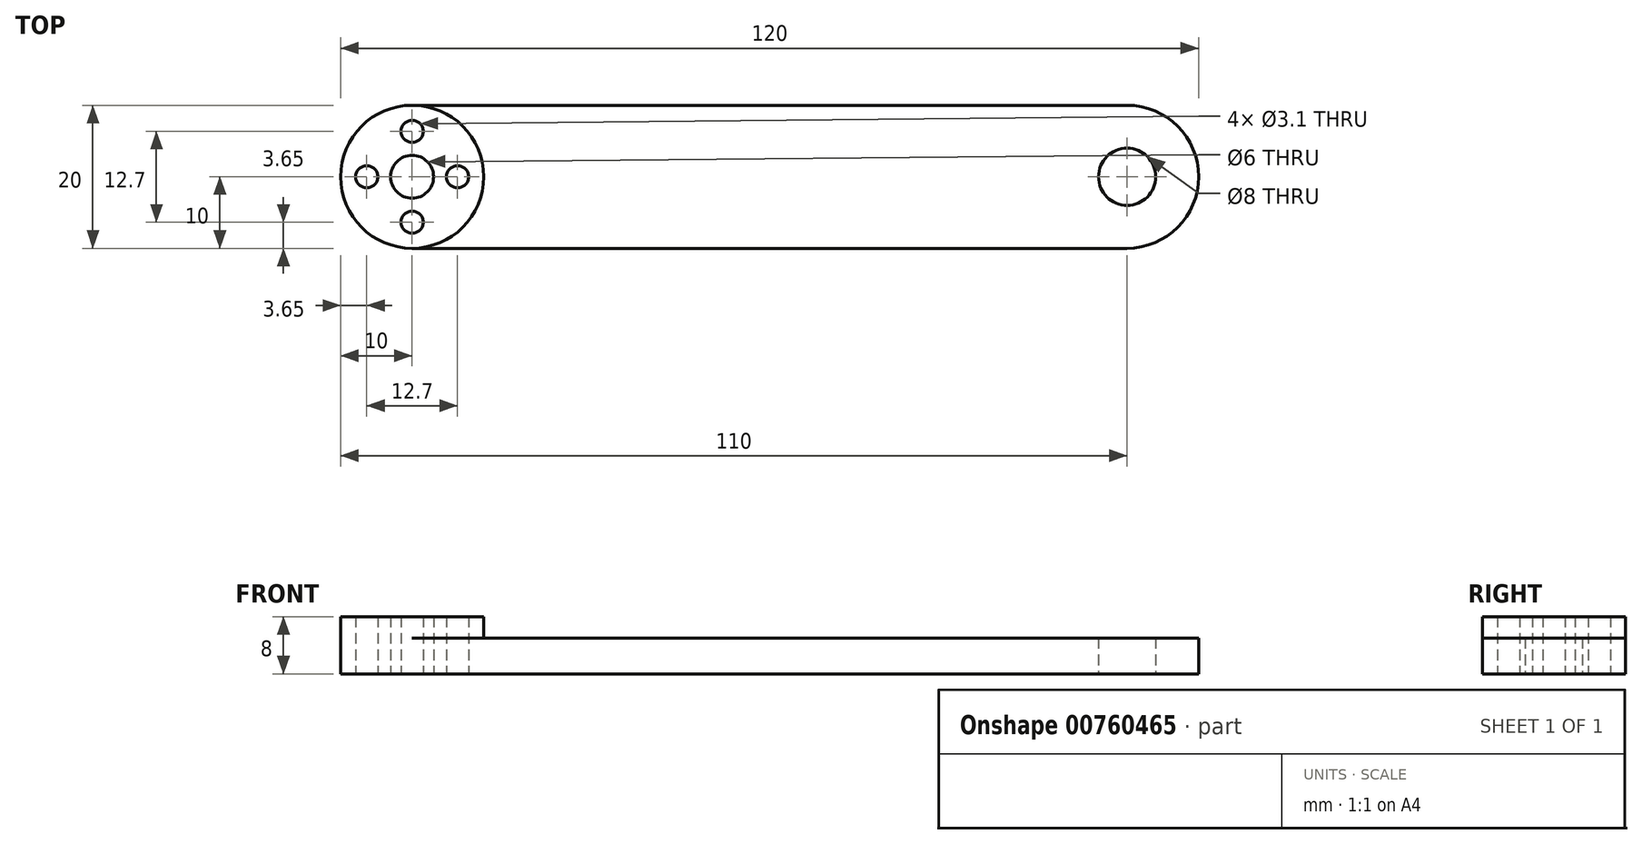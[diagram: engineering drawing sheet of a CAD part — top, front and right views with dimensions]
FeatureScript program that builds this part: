
annotation { "Feature Type Name" : "Feature", "Feature Type Description" : "" }
export const myFeature = defineFeature(function(context is Context, id is Id, definition is map)
    precondition{}
    {
        {
            var Q0;
            Q0=qCreatedBy(makeId("Top.planeOp"),FACE);
            var sketch = newSketch(context, id + "F0", { "sketchPlane" : qUnion([Q0])});
            skCircle(sketch, "E0", {"center": v(0, 0) * mm, "radius": 10 * mm});
            skCircle(sketch, "E1", {"center": v(6.35, 0) * mm, "radius": 1.55 * mm});
            skCircle(sketch, "E2.1.0", {"center": v(0, 6.35) * mm, "radius": 1.55 * mm});
            skCircle(sketch, "E2.2.0", {"center": v(-6.35, 0) * mm, "radius": 1.55 * mm});
            skCircle(sketch, "E2.3.0", {"center": v(0, -6.35) * mm, "radius": 1.55 * mm});
            skCircle(sketch, "E3", {"center": v(0, 0) * mm, "radius": 3 * mm});
            skLineSegment(sketch, "E4", {"start": v(0, 10) * mm, "end": v(100, 10) * mm});
            skLineSegment(sketch, "E5", {"start": v(0, 10) * mm, "end": v(0, 0) * mm, "construction": true});
            skLineSegment(sketch, "E6", {"start": v(0, 0) * mm, "end": v(-10, 0) * mm, "construction": true});
            skLineSegment(sketch, "E7.MirrorCS", {"start": v(0, -10) * mm, "end": v(100, -10) * mm});
            skCircle(sketch, "E8", {"center": v(100, 0) * mm, "radius": 10 * mm});
            skCircle(sketch, "E9", {"center": v(100, 0) * mm, "radius": 4 * mm});
            skLineSegment(sketch, "E10", {"start": v(100, -4) * mm, "end": v(9.17, -4) * mm});
            skLineSegment(sketch, "E11.MirrorCS", {"start": v(100, 4) * mm, "end": v(9.17, 4) * mm});
            skSolve(sketch);
        }
        {
            var Q0;
            Q0=makeQuery(id+"F0.imprint","IMPRINT",FACE,{"disambiguationData":[TD([[makeQuery(id+"F0.imprint","IMPRINT",EDGE,{"derivedFrom":sQuery(id+"F0.wireOp",EDGE,"E1")}),-1.0]])]});
            var Q1;
            {var subQ0=sQuery(id+"F0.wireOp",EDGE,"E4");Q1=makeQuery(id+"F0.imprint","IMPRINT",FACE,{"disambiguationData":[TD([[makeQuery(id+"F0.imprint","IMPRINT",EDGE,{"derivedFrom":subQ0}),-1.0]])]});}
            var Q2;
            {var subQ0=sQuery(id+"F0.wireOp",EDGE,"E8");var subQ1=makeQuery(id+"F0.imprint","INTERSECT",VERTEX,{"derivedFrom":[sQuery(id+"F0.wireOp",EDGE,"E4"),subQ0]});Q2=makeQuery(id+"F0.imprint","IMPRINT",FACE,{"disambiguationData":[TD([[makeQuery(id+"F0.imprint","IMPRINT",EDGE,{"disambiguationData":[TD([[subQ1,-1.0]])],"derivedFrom":subQ0}),1.0]])]});}
            var Q3;
            {var subQ0=sQuery(id+"F0.wireOp",EDGE,"E7.MirrorCS");Q3=makeQuery(id+"F0.imprint","IMPRINT",FACE,{"disambiguationData":[TD([[makeQuery(id+"F0.imprint","IMPRINT",EDGE,{"derivedFrom":subQ0}),1.0]])]});}
            var Q4;
            {var subQ0=sQuery(id+"F0.wireOp",EDGE,"E10");var subQ1=sQuery(id+"F0.wireOp",EDGE,"E0");var subQ2=makeQuery(id+"F0.imprint","INTERSECT",VERTEX,{"derivedFrom":[subQ1,subQ0]});Q4=makeQuery(id+"F0.imprint","IMPRINT",FACE,{"disambiguationData":[TD([[makeQuery(id+"F0.imprint","IMPRINT",EDGE,{"disambiguationData":[TD([[subQ2,-1.0]])],"derivedFrom":subQ1}),-1.0]])]});}
            var Q5;
            {var subQ0=sQuery(id+"F0.wireOp",EDGE,"E11.MirrorCS");var subQ1=sQuery(id+"F0.wireOp",EDGE,"E8");var subQ2=makeQuery(id+"F0.imprint","INTERSECT",VERTEX,{"derivedFrom":[subQ1,subQ0]});Q5=makeQuery(id+"F0.imprint","IMPRINT",FACE,{"disambiguationData":[TD([[makeQuery(id+"F0.imprint","IMPRINT",EDGE,{"disambiguationData":[TD([[subQ2,-1.0]])],"derivedFrom":subQ1}),1.0]])]});}
            extrude(context, id + "F1", {"entities" : qUnion([Q0, Q1, Q2, Q3, Q4, Q5]), "depth" : 5 * mm, "offsetDistance" : 25 * mm});
        }
        {
            var Q0;
            Q0=makeQuery(id+"F0.imprint","IMPRINT",FACE,{"disambiguationData":[TD([[makeQuery(id+"F0.imprint","IMPRINT",EDGE,{"derivedFrom":sQuery(id+"F0.wireOp",EDGE,"E1")}),-1.0]])]});
            extrude(context, id + "F2", {"entities" : qUnion([Q0]), "operationType" : NewBodyOperationType.ADD, "depth" : 8 * mm, "offsetDistance" : 25 * mm});
        }
    });
